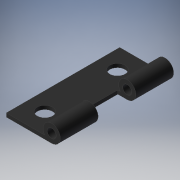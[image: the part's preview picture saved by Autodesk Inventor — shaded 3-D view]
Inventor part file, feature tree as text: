
AUTODESK INVENTOR PART (.ipt)
format: ipt  version: 2019 (Build 230136000, 136)  size: 143,360 bytes
history: native  units: mm
features: other x7, sketch x3, extrude x2, hole x1, pattern_linear x1
ambient origin geometry x8: Origin, YZ Plane, XZ Plane, XY Plane, X Axis, Y Axis, Z Axis, Center Point
bodies: Solid1 (feature_tree)
feature tree (14):
  extrude  "Extrusion1"  Depth=25.0mm TaperAngle=0.0deg
  extrude  "Extrusion2"  Depth=10.0mm TaperAngle=0.0deg
  hole  "Hole1"  [1 undecoded]
  pattern_linear  "Rectangular Pattern1"  [2 undecoded]
  other  "to_leaf1_XY"
  other  "to_leaf1_YZ"
  other  "to_leaf1_ZX"
  other  "to_leaf1_X"
  other  "to_leaf1_Y"
  other  "to_leaf1_Z"
  other  "to_leaf1_Center"
  sketch  "Sketch_15"  dims[d17=0.0mm]
  sketch  "Sketch_1"  dims[d0=25.0mm d1=0.0mm d2=3.8mm d3=0.0mm]
  sketch  "Sketch3"  dims[d4=3.4mm d5=6.0mm d6=4.0mm d7=2.0mm d8=90.0deg d9=0.8mm d10=0.0mm d11=20.0mm d13=16.0mm d14=10.0mm d16=0.0mm]
note: 3 required parameter values undecoded (feature->parameter linkage not recoverable at this tier; creation-order binding heuristic only, values carry confidence <= 0.55)
